# Revit family: CENTUM Profil XL 120s 6m vertikal L2D
name_source: partatom
category: HLS-Bauteile
units: mm (PartAtom-declared; Revit-internal decimal feet)

## family parameters
Arbeitsebenenbasiert = Ja
Beim Laden mit Abzugskörper schneiden = Nein
Bemaßung runder Anschluss = Durchmesser verwenden
Beschriftungsausrichtung beibehalten = Nein
Gemeinsam genutzt = Ja
Immer vertikal = Nein
Raumberechnungspunkt = Nein
Teiletyp = Normal

## types (1)
- Centum Profil XL120s L=6000 L2D
    Abmessung = 100/120/5.0 mm
    Artikelnummer = 16012061
    Breite = 100 mm  [stored 0.328084 ft]
    Bund = 72 m
    EAN = 4250928449382
    Fabrikat = MEFA
    Firma = MEFA Befestigungs- und Montagesysteme GmbH
    Fläche (schwächster Profilquerschnitt) = 0 m²
    Gewicht = 14,83 kg
    Höhe = 120 mm
    Kurztext1 = Montageprofil CENTUM XL 120s
    Kurztext2 = 100 / 120 / 5 mm L= 6 m fsv
    Langloch = 14.0 x 65.0 mm
    Länge = 6000 mm  [stored 19.685 ft]
    Material = Stahl
    Materialname = S275
    Mengeneinheit = m
    Oberflaeche = feuerstückverzinkt
    Profil = CENTUM
    Profiltyp = XL 120s
    Streckgrenze = 235 N/mm²
    Stärke = 5 mm  [stored 0.0164042 ft]
    Torsionswiderstandsmoment Wt = 109.25 cm³
    Trägheitsradius iy = 4.61 cm
    Trägheitsradius iz = 4.03 cm
    Vorgabe-Ansicht = 1219 mm
    Widerstandsmoment Wy = 62.12 cm³
    Widerstandsmoment Wz = 56.88 cm³
    vpe = 6

note: [stored X ft] marks values corroborated as IEEE doubles in the binary element streams (Revit-internal decimal feet)
